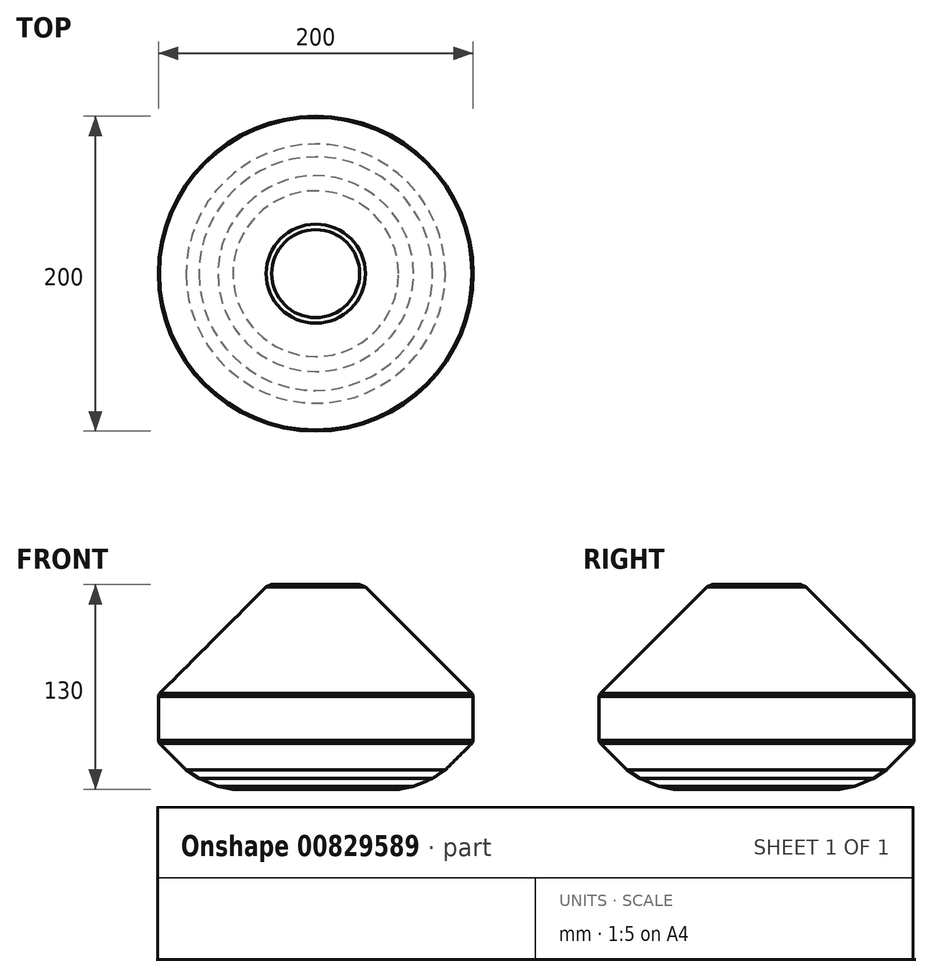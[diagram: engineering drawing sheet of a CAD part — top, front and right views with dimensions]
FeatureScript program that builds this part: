
annotation { "Feature Type Name" : "Feature", "Feature Type Description" : "" }
export const myFeature = defineFeature(function(context is Context, id is Id, definition is map)
    precondition{}
    {
        {
            var Q0;
            Q0=qCreatedBy(makeId("Top.planeOp"),FACE);
            var sketch = newSketch(context, id + "F0", { "sketchPlane" : qUnion([Q0])});
            skCircle(sketch, "E0", {"center": v(0, 0) * mm, "radius": 100 * mm});
            skSolve(sketch);
        }
        {
            var Q0;
            Q0=makeQuery(id+"F0.imprint","IMPRINT",FACE,{"disambiguationData":[TD([[makeQuery(id+"F0.imprint","IMPRINT",EDGE,{"derivedFrom":sQuery(id+"F0.wireOp",EDGE,"E0")}),1.0]])]});
            extrude(context, id + "F1", {"entities" : qUnion([Q0]), "depth" : 130 * mm, "offsetDistance" : 25 * mm});
        }
        {
            var Q0;
            Q0=makeQuery(id+"F1.opExtrude","CAP_FACE",FACE,{"disambiguationData":[OSD([sQuery(id+"F0.wireOp",EDGE,"E0")])],"isStart":false});
            chamfer(context, id + "F2", {"entities" : qUnion([Q0]), "chamferType" : ChamferType.TWO_OFFSETS, "width1" : 70 * mm, "oppositeDirection" : false, "width2" : 70 * mm, "tangentPropagation" : true});
        }
        {
            var Q0;
            Q0=makeQuery(id+"F1.opExtrude","CAP_FACE",FACE,{"disambiguationData":[OSD([sQuery(id+"F0.wireOp",EDGE,"E0")])],"isStart":true});
            chamfer(context, id + "F3", {"entities" : qUnion([Q0]), "width" : 30 * mm, "tangentPropagation" : true});
        }
        {
            var Q0;
            Q0=makeQuery(id+"F1.opExtrude","CAP_FACE",FACE,{"disambiguationData":[OSD([sQuery(id+"F0.wireOp",EDGE,"E0")])],"isStart":true});
            chamfer(context, id + "F4", {"entities" : qUnion([Q0]), "width" : 30 * mm, "tangentPropagation" : true});
        }
        {
            var Q0;
            Q0=makeQuery(id+"F4.opChamfer","BLEND_FACE",FACE,{"disambiguationData":[OSD([sQuery(id+"F0.wireOp",EDGE,"E0")])]});
            chamfer(context, id + "F5", {"entities" : qUnion([Q0]), "width" : 25 * mm, "tangentPropagation" : true});
        }
        {
            var Q0;
            Q0=makeQuery(id+"F1.opExtrude","SWEPT_FACE",FACE,{"disambiguationData":[OSD([sQuery(id+"F0.wireOp",EDGE,"E0")])]});
            chamfer(context, id + "F6", {"entities" : qUnion([Q0]), "width" : 2.5 * mm, "tangentPropagation" : true});
        }
        {
            var Q0;
            Q0=makeQuery(id+"F1.opExtrude","CAP_FACE",FACE,{"disambiguationData":[OSD([sQuery(id+"F0.wireOp",EDGE,"E0")])],"isStart":false});
            chamfer(context, id + "F7", {"entities" : qUnion([Q0]), "width" : 5 * mm, "tangentPropagation" : true});
        }
    });
